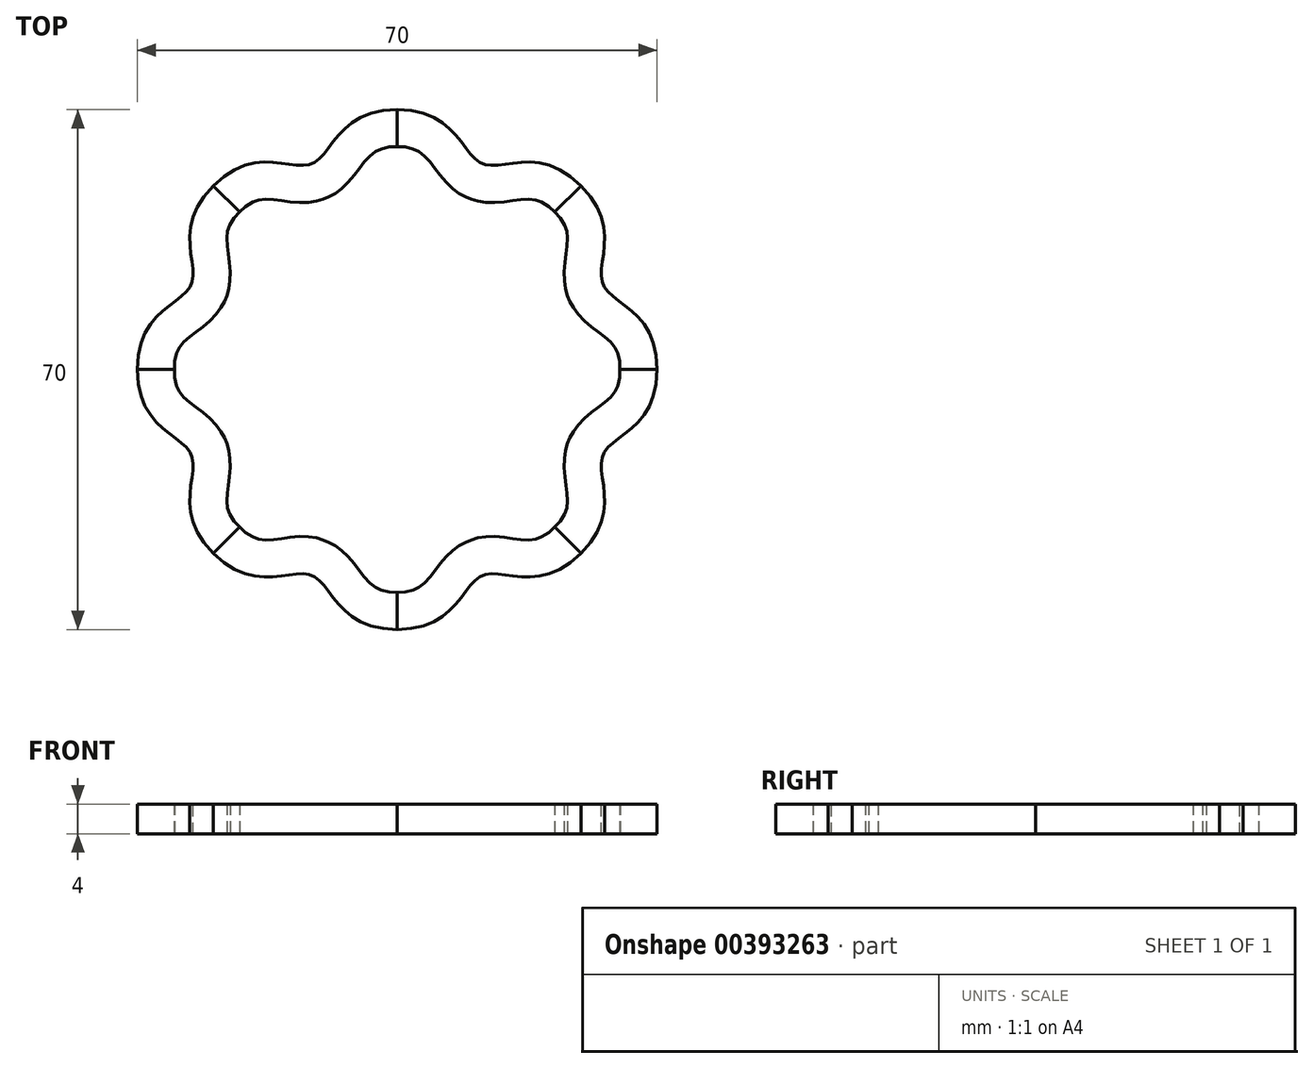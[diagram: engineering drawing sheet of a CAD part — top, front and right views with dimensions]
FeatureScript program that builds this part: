
annotation { "Feature Type Name" : "Feature", "Feature Type Description" : "" }
export const myFeature = defineFeature(function(context is Context, id is Id, definition is map)
    precondition{}
    {
        {
            var Q0;
            Q0=qCreatedBy(makeId("Top.planeOp"),FACE);
            var sketch = newSketch(context, id + "F0", { "sketchPlane" : qUnion([Q0])});
            skLineSegment(sketch, "E0", {"start": v(0, 0) * mm, "end": v(13.4, 32.34) * mm, "construction": true});
            skLineSegment(sketch, "E1", {"start": v(-15.7, 35) * mm, "end": v(11.65, 35) * mm, "construction": true});
            skLineSegment(sketch, "E2", {"start": v(24.75, 24.75) * mm, "end": v(13.44, 36.06) * mm, "construction": true});
            skFitSpline(sketch, "E3", {"points": [v(0, 35) * mm, v(11.48, 27.72) * mm, v(24.75, 24.75) * mm], "startDerivative": vector(48, 0) * mm, "endDerivative": vector(33.94, -33.94) * mm});
            skFitSpline(sketch, "E4.0", {"points": [v(0, 30) * mm, v(0.68, 30) * mm, v(1.47, 29.9) * mm, v(2.2, 29.7) * mm, v(2.63, 29.52) * mm, v(2.99, 29.32) * mm, v(3.43, 29) * mm, v(3.87, 28.58) * mm, v(4.36, 28.01) * mm, v(4.76, 27.5) * mm, v(5.2, 26.92) * mm, v(5.7, 26.26) * mm, v(6.3, 25.51) * mm, v(6.95, 24.83) * mm, v(7.6, 24.27) * mm, v(8.16, 23.84) * mm, v(8.7, 23.51) * mm, v(9.18, 23.26) * mm, v(9.57, 23.1) * mm, v(9.96, 22.94) * mm, v(10.47, 22.78) * mm, v(11.09, 22.63) * mm, v(11.78, 22.53) * mm, v(12.64, 22.47) * mm, v(13.58, 22.5) * mm, v(14.54, 22.6) * mm, v(15.36, 22.7) * mm, v(16.08, 22.81) * mm, v(16.72, 22.9) * mm, v(17.47, 22.95) * mm, v(18.08, 22.93) * mm, v(18.62, 22.84) * mm, v(19.02, 22.73) * mm, v(19.45, 22.55) * mm, v(20.1, 22.19) * mm, v(20.73, 21.7) * mm, v(21.21, 21.21) * mm]});
            skLineSegment(sketch, "E5", {"start": v(0, 30) * mm, "end": v(0, 35) * mm});
            skLineSegment(sketch, "E6", {"start": v(21.21, 21.21) * mm, "end": v(24.75, 24.75) * mm});
            skSolve(sketch);
        }
        {
            var Q0;
            Q0 = qSketchRegion(id + "F0", true);
            extrude(context, id + "F1", {"entities" : qUnion([Q0]), "depth" : 4 * mm});
        }
        {
            var Q0;
            Q0=qCreatedBy(makeId("Front.planeOp"),FACE);
            var sketch = newSketch(context, id + "F2", { "sketchPlane" : qUnion([Q0])});
            skLineSegment(sketch, "E7", {"start": v(0, 0) * mm, "end": v(0, 46.86) * mm});
            skSolve(sketch);
        }
        {
            var Q0;
            Q0=makeQuery(id+"F1.opExtrude","SWEPT_BODY",BODY,{"disambiguationData":[OSD([sQuery(id+"F0.wireOp",EDGE,"E3"),sQuery(id+"F0.wireOp",EDGE,"E4.0"),sQuery(id+"F0.wireOp",EDGE,"E5"),sQuery(id+"F0.wireOp",EDGE,"E6")])]});
            var Q1;
            Q1=sQuery(id+"F2.wireOp",EDGE,"E7");
            circularPattern(context, id + "F3", {"entities" : qUnion([Q0]), "axis" : qUnion([Q1]), "angle" : 360 * degree, "instanceCount" : 8, "equalSpace" : true});
        }
    });
